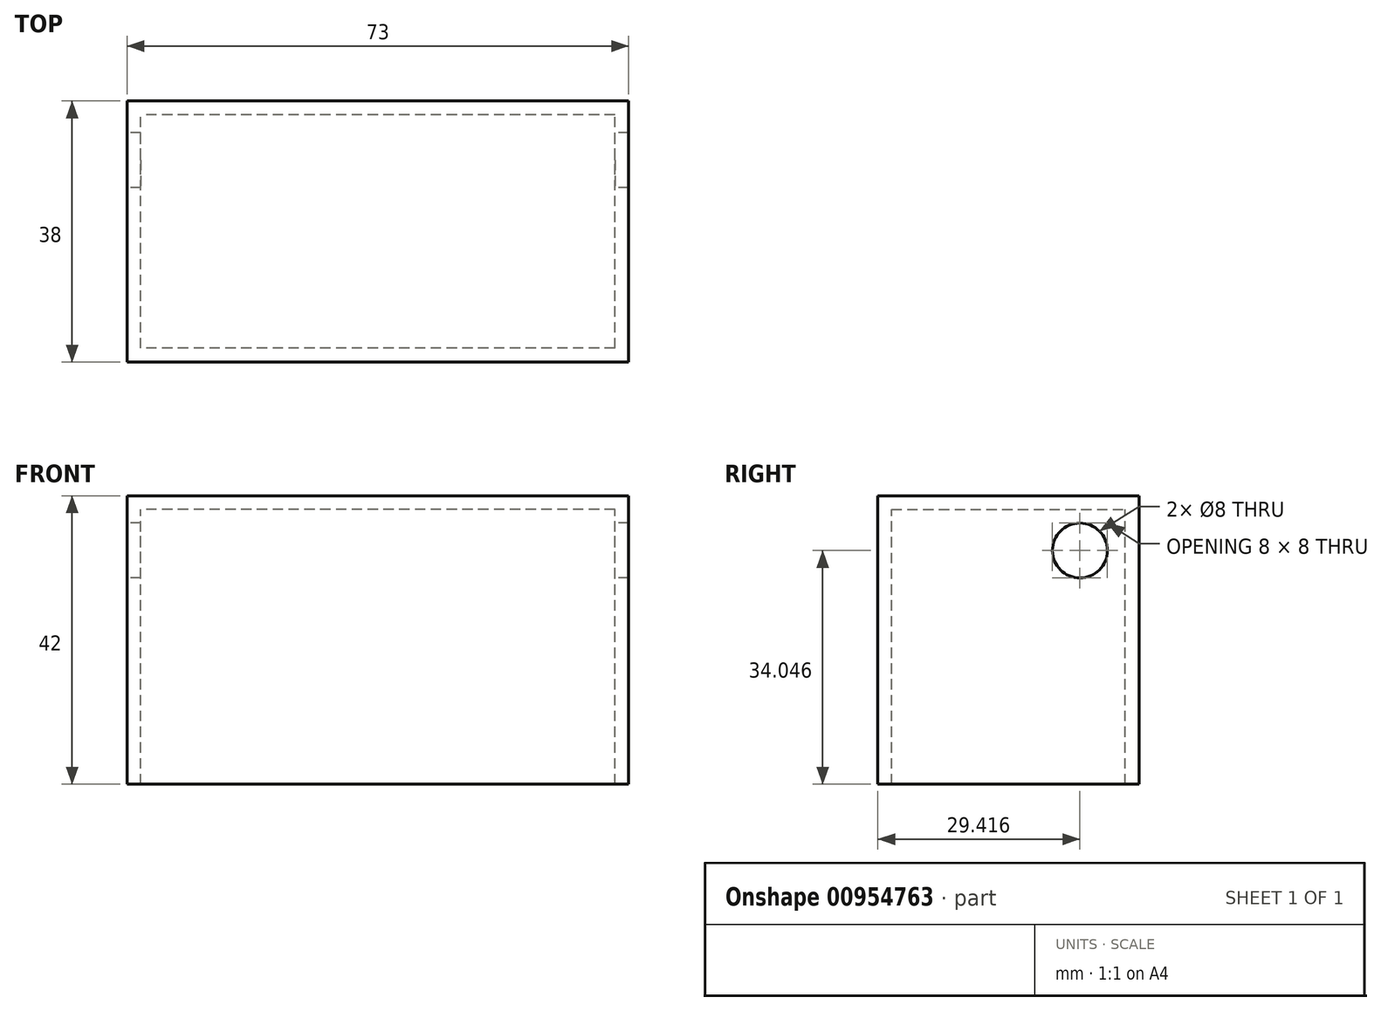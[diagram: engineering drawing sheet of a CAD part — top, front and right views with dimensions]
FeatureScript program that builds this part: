
annotation { "Feature Type Name" : "Feature", "Feature Type Description" : "" }
export const myFeature = defineFeature(function(context is Context, id is Id, definition is map)
    precondition{}
    {
        {
            var Q0;
            Q0=qCreatedBy(makeId("Top.planeOp"),FACE);
            var sketch = newSketch(context, id + "F0", { "sketchPlane" : qUnion([Q0])});
            skLineSegment(sketch, "E0.bottom", {"start": v(34.5, -17) * mm, "end": v(-34.5, -17) * mm});
            skLineSegment(sketch, "E0.top", {"start": v(34.5, 17) * mm, "end": v(-34.5, 17) * mm});
            skLineSegment(sketch, "E0.left", {"start": v(34.5, -17) * mm, "end": v(34.5, 17) * mm});
            skLineSegment(sketch, "E0.right", {"start": v(-34.5, -17) * mm, "end": v(-34.5, 17) * mm});
            skPoint(sketch, "E0.middle", {"position": v(0, 0) * mm});
            skLineSegment(sketch, "E1.bottom", {"start": v(36.5, -19) * mm, "end": v(-36.5, -19) * mm});
            skLineSegment(sketch, "E1.top", {"start": v(36.5, 19) * mm, "end": v(-36.5, 19) * mm});
            skLineSegment(sketch, "E1.left", {"start": v(36.5, -19) * mm, "end": v(36.5, 19) * mm});
            skLineSegment(sketch, "E1.right", {"start": v(-36.5, -19) * mm, "end": v(-36.5, 19) * mm});
            skSolve(sketch);
        }
        {
            var Q0;
            Q0=makeQuery(id+"F0.imprint","IMPRINT",FACE,{"disambiguationData":[TD([[makeQuery(id+"F0.imprint","IMPRINT",EDGE,{"derivedFrom":sQuery(id+"F0.wireOp",EDGE,"E0.bottom")}),1.0]])]});
            var Q1;
            Q1=makeQuery(id+"F0.imprint","IMPRINT",FACE,{"disambiguationData":[TD([[makeQuery(id+"F0.imprint","IMPRINT",EDGE,{"derivedFrom":sQuery(id+"F0.wireOp",EDGE,"E0.bottom")}),-1.0]])]});
            extrude(context, id + "F1", {"entities" : qUnion([Q0, Q1]), "depth" : 2 * mm, "offsetDistance" : 25 * mm});
        }
        {
            var Q0;
            Q0=makeQuery(id+"F0.imprint","IMPRINT",FACE,{"disambiguationData":[TD([[makeQuery(id+"F0.imprint","IMPRINT",EDGE,{"derivedFrom":sQuery(id+"F0.wireOp",EDGE,"E0.bottom")}),1.0]])]});
            extrude(context, id + "F2", {"entities" : qUnion([Q0]), "operationType" : NewBodyOperationType.ADD, "oppositeDirection" : true, "depth" : 40 * mm, "offsetDistance" : 25 * mm});
        }
        {
            var Q0;
            {var subQ0=sQuery(id+"F0.wireOp",EDGE,"E1.right");Q0=makeQuery(id+"F2.boolean.opBoolean","MERGE",FACE,{"derivedFrom":[makeQuery(id+"F1.opExtrude","SWEPT_FACE",FACE,{"disambiguationData":[OSD([subQ0])]}),makeQuery(id+"F2.opExtrude","SWEPT_FACE",FACE,{"disambiguationData":[OSD([subQ0])]})]});}
            var sketch = newSketch(context, id + "F3", { "sketchPlane" : qUnion([Q0])});
            skCircle(sketch, "E2", {"center": v(-10.42, -5.95) * mm, "radius": 4 * mm});
            skSolve(sketch);
        }
        {
            var Q0;
            Q0=makeQuery(id+"F3.imprint","IMPRINT",FACE,{"disambiguationData":[TD([[makeQuery(id+"F3.imprint","IMPRINT",EDGE,{"derivedFrom":sQuery(id+"F3.wireOp",EDGE,"E2")}),1.0]])]});
            extrude(context, id + "F4", {"entities" : qUnion([Q0]), "operationType" : NewBodyOperationType.REMOVE, "endBound" : BoundingType.THROUGH_ALL, "oppositeDirection" : true, "depth" : 25 * mm, "offsetDistance" : 25 * mm});
        }
    });
